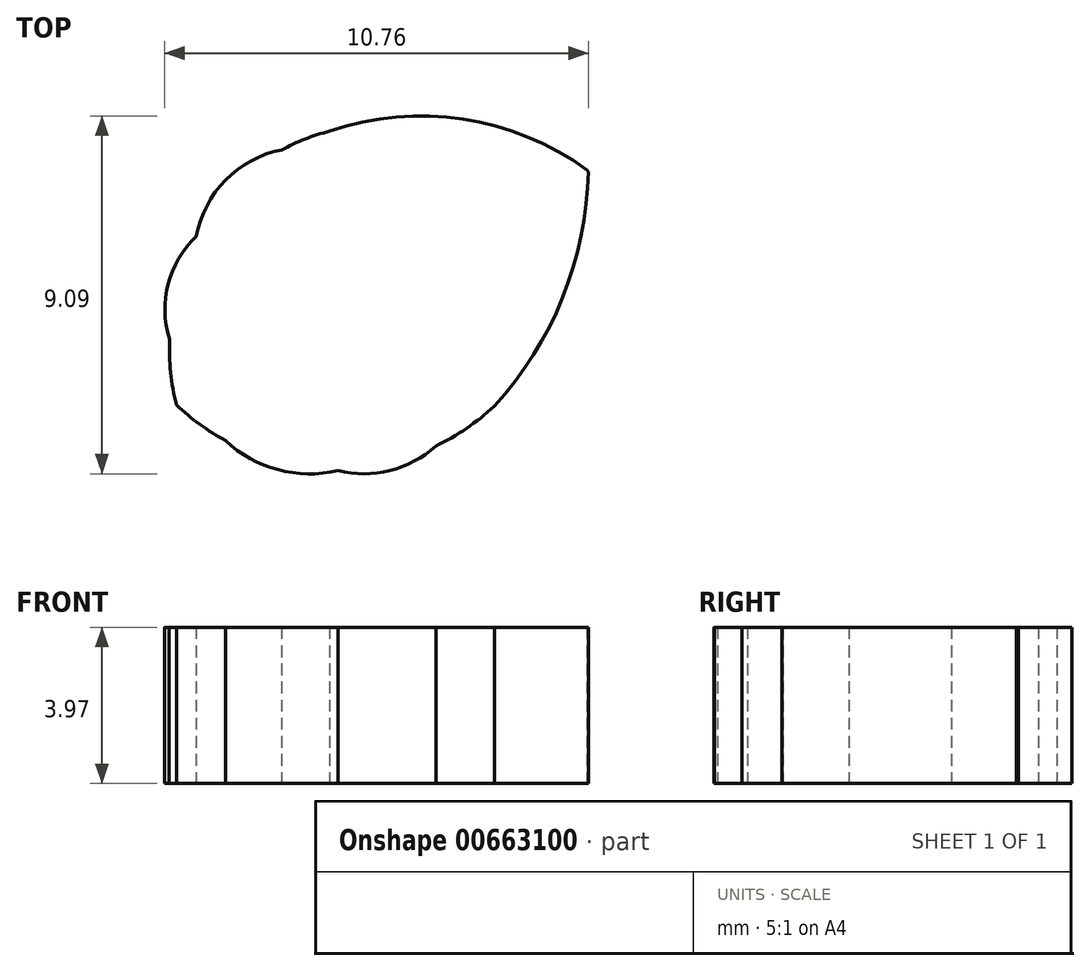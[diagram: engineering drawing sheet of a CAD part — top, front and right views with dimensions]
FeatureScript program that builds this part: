
annotation { "Feature Type Name" : "Feature", "Feature Type Description" : "" }
export const myFeature = defineFeature(function(context is Context, id is Id, definition is map)
    precondition{}
    {
        {
            var Q0;
            Q0=qCreatedBy(makeId("Top.planeOp"),FACE);
            var sketch = newSketch(context, id + "F0", { "sketchPlane" : qUnion([Q0])});
            skPoint(sketch, "E0.center", {"position": v(0, 0) * mm});
            skPoint(sketch, "E1.center", {"position": v(-0.03, 0.1) * mm});
            skLineSegment(sketch, "E2", {"start": v(-12.37, 4.64) * mm, "end": v(-12.37, 4.57) * mm});
            skLineSegment(sketch, "E3", {"start": v(7.76, 1.05) * mm, "end": v(7.76, 1.05) * mm});
            skLineSegment(sketch, "E4", {"start": v(8, -1.42) * mm, "end": v(8, -1.42) * mm});
            skLineSegment(sketch, "E5", {"start": v(6.33, 3.65) * mm, "end": v(6.36, 3.6) * mm});
            skArc(sketch, "E6", {"start": v(3.97, -2.35) * mm, "mid": v(5.7, 0.4) * mm, "end": v(6.36, 3.6) * mm});
            skArc(sketch, "E7", {"start": v(6.33, 3.65) * mm, "mid": v(3.18, 4.94) * mm, "end": v(-0.21, 4.63) * mm});
            skArc(sketch, "E8", {"start": v(-4.1, -2.33) * mm, "mid": v(-3.51, -2.81) * mm, "end": v(-2.86, -3.23) * mm});
            skArc(sketch, "E9", {"start": v(2.48, -3.37) * mm, "mid": v(3.26, -2.92) * mm, "end": v(3.97, -2.35) * mm});
            skArc(sketch, "E10", {"start": v(-2.86, -3.23) * mm, "mid": v(-1.53, -3.97) * mm, "end": v(0, -4) * mm});
            skArc(sketch, "E11", {"start": v(0, -4) * mm, "mid": v(1.32, -3.99) * mm, "end": v(2.48, -3.37) * mm});
            skArc(sketch, "E12", {"start": v(-4.28, -0.65) * mm, "mid": v(-4.25, -1.5) * mm, "end": v(-4.1, -2.33) * mm});
            skArc(sketch, "E13", {"start": v(-3.6, 1.96) * mm, "mid": v(-4.32, 0.75) * mm, "end": v(-4.28, -0.65) * mm});
            skArc(sketch, "E14", {"start": v(-0.21, 4.63) * mm, "mid": v(-0.84, 4.43) * mm, "end": v(-1.43, 4.16) * mm});
            skArc(sketch, "E15", {"start": v(-1.43, 4.16) * mm, "mid": v(-2.86, 3.4) * mm, "end": v(-3.6, 1.96) * mm});
            skSolve(sketch);
        }
        {
            var Q0;
            Q0=makeQuery(id+"F0.imprint","IMPRINT",FACE,{"disambiguationData":[TD([[makeQuery(id+"F0.imprint","IMPRINT",EDGE,{"derivedFrom":sQuery(id+"F0.wireOp",EDGE,"E5")}),-1.0]])]});
            extrude(context, id + "F1", {"entities" : qUnion([Q0]), "depth" : 3.97 * mm, "offsetDistance" : 25.4 * mm});
        }
    });
